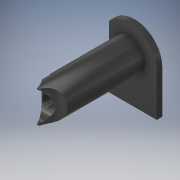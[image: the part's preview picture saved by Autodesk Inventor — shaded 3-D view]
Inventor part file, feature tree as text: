
AUTODESK INVENTOR PART (.ipt)
format: ipt  version: 2017 (Build 210142000, 142)  size: 179,712 bytes
history: native  units: in
note: dims shown in document units (in); Inventor stores cm internally (conversion verified against a paired STEP export)
features: extrude x7, sketch x7, chamfer x1
ambient origin geometry x8: Origin, YZ Plane, XZ Plane, XY Plane, X Axis, Y Axis, Z Axis, Center Point
bodies: Solid1 (feature_tree)
feature tree (15):
  extrude  "Extrusion1"  Depth=0.8661in TaperAngle=0.0deg
  extrude  "Extrusion2"  Depth=0.1811in
  extrude  "Extrusion3"  Depth=0.0492in TaperAngle=0.0deg
  extrude  "Extrusion4"  Depth=0.6299in TaperAngle=0.0deg
  chamfer  "Chamfer1"  Distance=0.6299in
  extrude  "Extrusion5"  Depth=0.2136in
  extrude  "Extrusion6"  TaperAngle=0.0deg  [1 undecoded]
  extrude  "Extrusion7"  TaperAngle=30.0deg  [1 undecoded]
  sketch  "Sketch1"  dims[d0=0.2854in d1=0.8661in d2=0.0in]
  sketch  "Sketch2"  dims[d3=0.248in d4=0.1811in]
  sketch  "Sketch3"  dims[d5=0.3858in d6=0.0492in d7=0.0in]
  sketch  "Sketch4"  dims[d8=0.1732in d9=0.6299in d10=0.0in]
  sketch  "Sketch5"  dims[d11=0.0984in d12=0.6299in d13=0.0in]
  sketch  "Sketch6"  dims[d14=0.0551in d15=0.0787in d16=45.0deg d17=0.2136in]
  sketch  "Sketch7"  dims[d18=0.6693in d19=0.0in d20=0.0in d21=30.0deg d22=0.1811in d23=0.2126in d24=0.0551in d25=0.0in d26=0.0in d27=0.6299in d28=0.0in d29=0.0118in]
note: 2 required parameter values undecoded (feature->parameter linkage not recoverable at this tier; creation-order binding heuristic only, values carry confidence <= 0.55)
